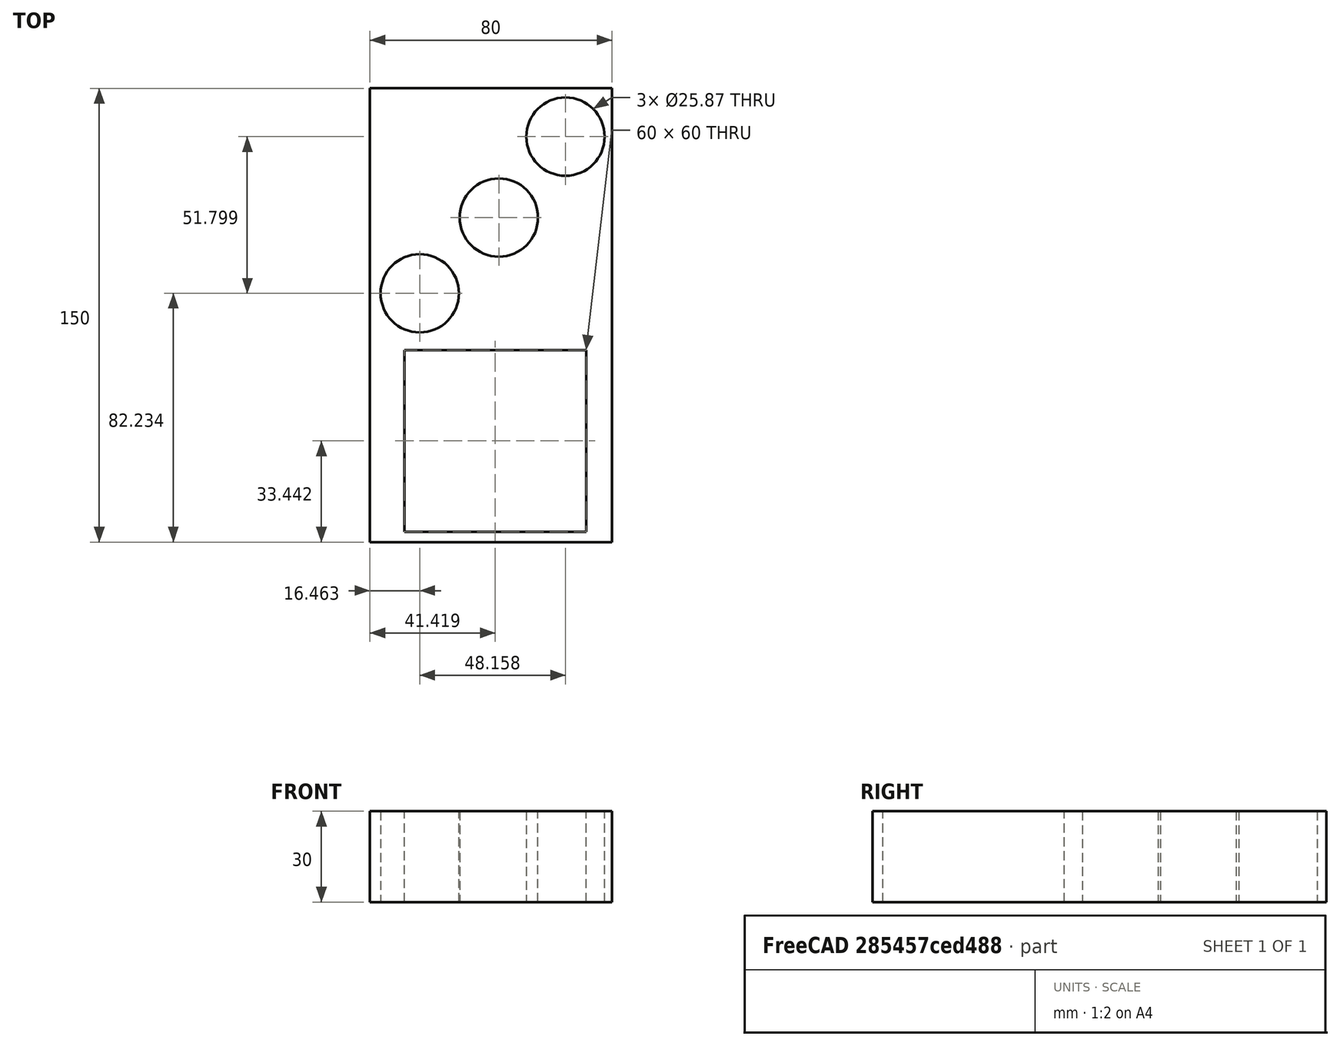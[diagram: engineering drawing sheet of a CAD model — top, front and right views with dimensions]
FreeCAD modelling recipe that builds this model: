
FCSTD DOCUMENT  (FreeCAD 0.18R16131 (Git))
Label: Momentum_Main_Plate_30X80X150
License: All rights reserved
LicenseURL: http://en.wikipedia.org/wiki/All_rights_reserved
objects: Sketcher::SketchObject×1, PartDesign::Pad×1, PartDesign::Body×1
note: 4 computed .brp shape members not serialized (recipe doc carries the construction recipe); baked Part::Feature solids carry a one-line shape summary decoded from their .brp

FEATURE [Sketcher::SketchObject] Sketch
  MapMode = 5
  Support = -> [XY_Plane]
  sketch-geometry (11):
    g0: LineSegment StartX=-58.6841 StartY=-53.0777 StartZ=0 EndX=21.3159 EndY=-53.0777 EndZ=0
    g1: LineSegment StartX=21.3159 StartY=-53.0777 StartZ=0 EndX=21.3159 EndY=96.9223 EndZ=0
    g2: LineSegment StartX=21.3159 StartY=96.9223 StartZ=0 EndX=-58.6841 EndY=96.9223 EndZ=0
    g3: LineSegment StartX=-58.6841 StartY=96.9223 StartZ=0 EndX=-58.6841 EndY=-53.0777 EndZ=0
    g4: LineSegment StartX=-47.2611 StartY=-49.6384 StartZ=0 EndX=12.7389 EndY=-49.6384 EndZ=0
    g5: LineSegment StartX=12.7389 StartY=-49.6384 StartZ=0 EndX=12.7389 EndY=10.3616 EndZ=0
    g6: LineSegment StartX=12.7389 StartY=10.3616 StartZ=0 EndX=-47.2611 EndY=10.3616 EndZ=0
    g7: LineSegment StartX=-47.2611 StartY=10.3616 StartZ=0 EndX=-47.2611 EndY=-49.6384 EndZ=0
    g8: Circle CenterX=-42.2166 CenterY=29.154 CenterZ=0 NormalX=0 NormalY=0 NormalZ=1 AngleXU=0 Radius=12.9349
    g9: Circle CenterX=-16.0723 CenterY=54.191 CenterZ=0 NormalX=0 NormalY=0 NormalZ=1 AngleXU=0 Radius=12.9349
    g10: Circle CenterX=5.94154 CenterY=80.9529 CenterZ=0 NormalX=0 NormalY=0 NormalZ=1 AngleXU=0 Radius=12.9349
  constraints (20):
    c: Coincident(g0,g1)
    c: Coincident(g1,g2)
    c: Coincident(g2,g3)
    c: Coincident(g3,g0)
    c: Horizontal(g0)
    c: Horizontal(g2)
    c: Vertical(g1)
    c: Vertical(g3)
    c: DistanceX(g0,g0) = 80
    c: DistanceY(g1,g1) = 150
    c: Coincident(g4,g5)
    c: Coincident(g5,g6)
    c: Coincident(g6,g7)
    c: Coincident(g7,g4)
    c: Horizontal(g4)
    c: Horizontal(g6)
    c: Vertical(g5)
    c: Vertical(g7)
    c: DistanceX(g4,g4) = 60
    c: DistanceY(g5,g5) = 60
FEATURE [PartDesign::Pad] Pad
  Length = 30
  Length2 = 100
  Profile = -> Sketch
  Type = 0
FEATURE [PartDesign::Body] Body
  Group = -> [Sketch,Pad]
  Origin = -> Origin
  Tip = -> Pad
